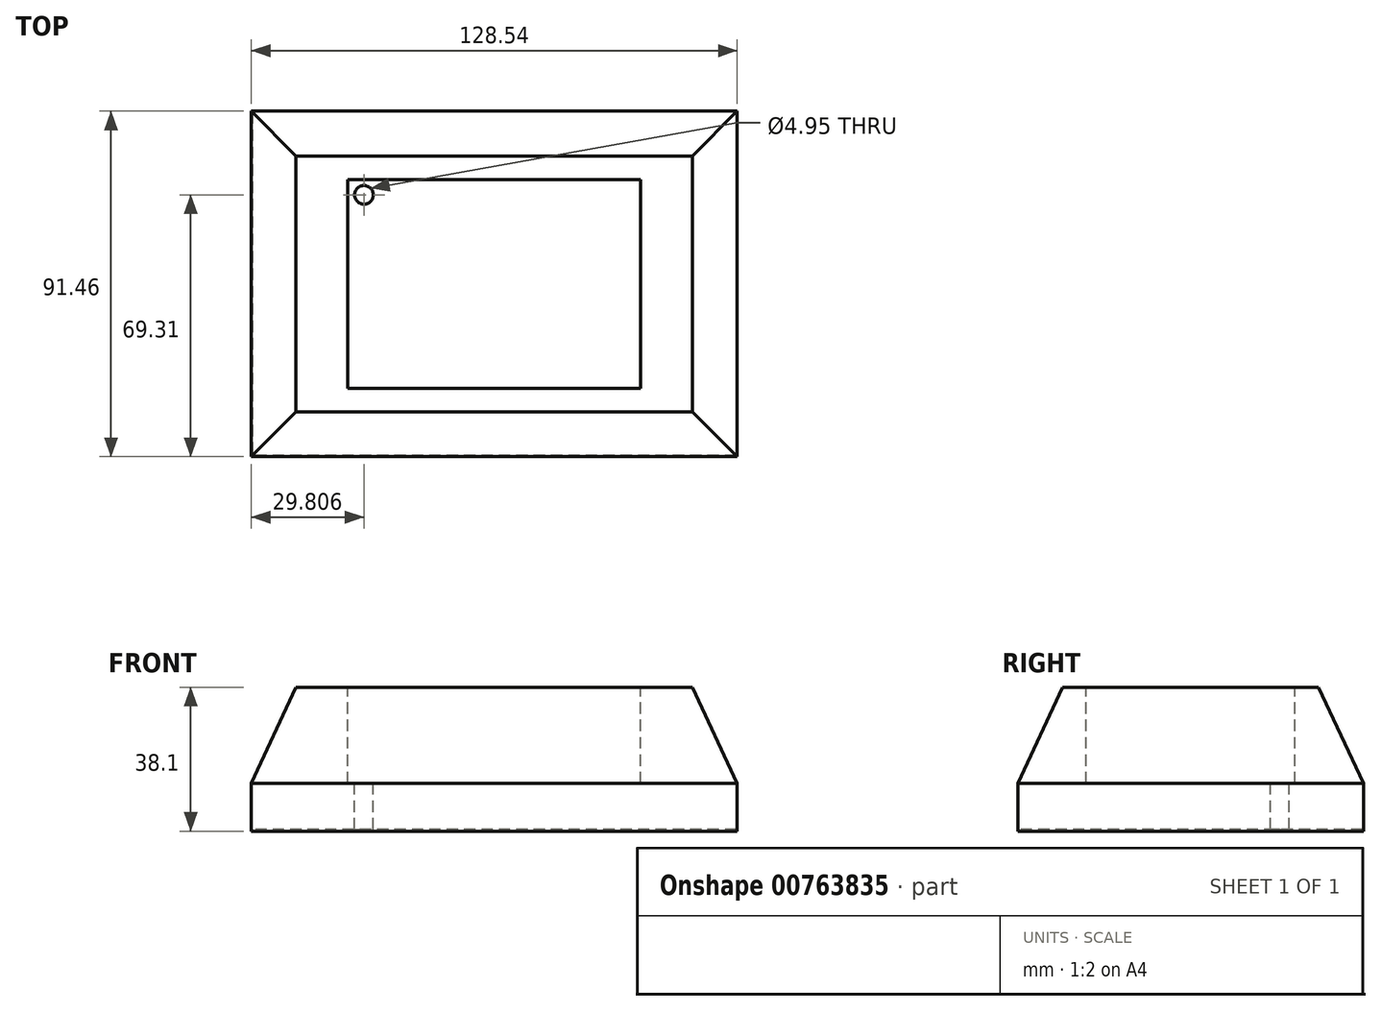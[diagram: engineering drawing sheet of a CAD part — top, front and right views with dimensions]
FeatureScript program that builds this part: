
annotation { "Feature Type Name" : "Feature", "Feature Type Description" : "" }
export const myFeature = defineFeature(function(context is Context, id is Id, definition is map)
    precondition{}
    {
        {
            var Q0;
            Q0=qCreatedBy(makeId("Top.planeOp"),FACE);
            var sketch = newSketch(context, id + "F0", { "sketchPlane" : qUnion([Q0])});
            skLineSegment(sketch, "E0.bottom", {"start": v(64.27, 45.73) * mm, "end": v(-64.27, 45.73) * mm});
            skLineSegment(sketch, "E0.top", {"start": v(64.27, -45.73) * mm, "end": v(-64.27, -45.73) * mm});
            skLineSegment(sketch, "E0.left", {"start": v(64.27, 45.73) * mm, "end": v(64.27, -45.73) * mm});
            skLineSegment(sketch, "E0.right", {"start": v(-64.27, 45.73) * mm, "end": v(-64.27, -45.73) * mm});
            skPoint(sketch, "E0.middle", {"position": v(0, 0) * mm});
            skSolve(sketch);
        }
        {
            var Q0;
            Q0=makeQuery(id+"F0.imprint","IMPRINT",FACE,{"disambiguationData":[TD([[makeQuery(id+"F0.imprint","IMPRINT",EDGE,{"derivedFrom":sQuery(id+"F0.wireOp",EDGE,"E0.bottom")}),1.0]])]});
            extrude(context, id + "F1", {"entities" : qUnion([Q0]), "depth" : 12.7 * mm, "offsetDistance" : 25.4 * mm});
        }
        {
            var Q0;
            Q0=makeQuery(id+"F1.opExtrude","CAP_FACE",FACE,{"disambiguationData":[OSD([sQuery(id+"F0.wireOp",EDGE,"E0.bottom"),sQuery(id+"F0.wireOp",EDGE,"E0.top"),sQuery(id+"F0.wireOp",EDGE,"E0.left"),sQuery(id+"F0.wireOp",EDGE,"E0.right")])],"isStart":false});
            extrude(context, id + "F2", {"entities" : qUnion([Q0]), "operationType" : NewBodyOperationType.ADD, "depth" : 25.4 * mm, "offsetDistance" : 25.4 * mm, "hasDraft" : true, "draftAngle" : 25 * degree, "draftPullDirection" : true});
        }
        {
            var Q0;
            Q0=makeQuery(id+"F1.opExtrude","CAP_FACE",FACE,{"disambiguationData":[OSD([sQuery(id+"F0.wireOp",EDGE,"E0.bottom"),sQuery(id+"F0.wireOp",EDGE,"E0.top"),sQuery(id+"F0.wireOp",EDGE,"E0.left"),sQuery(id+"F0.wireOp",EDGE,"E0.right")])],"isStart":true});
            var sketch = newSketch(context, id + "F3", { "sketchPlane" : qUnion([Q0])});
            skLineSegment(sketch, "E1.0", {"start": v(64.02, -45.48) * mm, "end": v(-64.27, -45.48) * mm});
            skLineSegment(sketch, "E1.1", {"start": v(64.02, -45.48) * mm, "end": v(64.02, 45.48) * mm});
            skLineSegment(sketch, "E1.2", {"start": v(64.02, 45.48) * mm, "end": v(-64.27, 45.48) * mm});
            skLineSegment(sketch, "E2.0", {"start": v(-64.02, -45.73) * mm, "end": v(-64.02, 45.73) * mm});
            skSolve(sketch);
        }
        {
            var Q0;
            Q0 = qSketchRegion(id + "F3", true);
            extrude(context, id + "F4", {"entities" : qUnion([Q0]), "operationType" : NewBodyOperationType.REMOVE, "oppositeDirection" : true, "depth" : 0.5 * mm, "offsetDistance" : 25.4 * mm});
        }
        {
            var Q0;
            Q0=makeQuery(id+"F2.opExtrude","CAP_FACE",FACE,{"disambiguationData":[OSD([sQuery(id+"F0.wireOp",EDGE,"E0.bottom"),sQuery(id+"F0.wireOp",EDGE,"E0.top"),sQuery(id+"F0.wireOp",EDGE,"E0.left"),sQuery(id+"F0.wireOp",EDGE,"E0.right")])],"isStart":false});
            var sketch = newSketch(context, id + "F5", { "sketchPlane" : qUnion([Q0])});
            skLineSegment(sketch, "E3.bottom", {"start": v(38.7, 27.61) * mm, "end": v(-38.7, 27.61) * mm});
            skLineSegment(sketch, "E3.top", {"start": v(38.7, -27.61) * mm, "end": v(-38.7, -27.61) * mm});
            skLineSegment(sketch, "E3.left", {"start": v(38.7, 27.61) * mm, "end": v(38.7, -27.61) * mm});
            skLineSegment(sketch, "E3.right", {"start": v(-38.7, 27.61) * mm, "end": v(-38.7, -27.61) * mm});
            skPoint(sketch, "E3.middle", {"position": v(0, 0) * mm});
            skSolve(sketch);
        }
        {
            var Q0;
            Q0=makeQuery(id+"F5.imprint","IMPRINT",FACE,{"disambiguationData":[TD([[makeQuery(id+"F5.imprint","IMPRINT",EDGE,{"derivedFrom":sQuery(id+"F5.wireOp",EDGE,"E3.bottom")}),1.0]])]});
            extrude(context, id + "F6", {"entities" : qUnion([Q0]), "operationType" : NewBodyOperationType.REMOVE, "oppositeDirection" : true, "depth" : 25.4 * mm, "offsetDistance" : 25.4 * mm});
        }
        {
            var Q0;
            Q0=makeQuery(id+"F6.boolean.opBoolean","COPY",FACE,{"derivedFrom":makeQuery(id+"F6.opExtrude","CAP_FACE",FACE,{"disambiguationData":[OSD([sQuery(id+"F5.wireOp",EDGE,"E3.bottom"),sQuery(id+"F5.wireOp",EDGE,"E3.top"),sQuery(id+"F5.wireOp",EDGE,"E3.left"),sQuery(id+"F5.wireOp",EDGE,"E3.right")])],"isStart":false})});
            var sketch = newSketch(context, id + "F7", { "sketchPlane" : qUnion([Q0])});
            skCircle(sketch, "E4", {"center": v(-34.46, 23.58) * mm, "radius": 2.47 * mm});
            skSolve(sketch);
        }
        {
            var Q0;
            Q0=makeQuery(id+"F7.imprint","IMPRINT",FACE,{"disambiguationData":[TD([[makeQuery(id+"F7.imprint","IMPRINT",EDGE,{"derivedFrom":sQuery(id+"F7.wireOp",EDGE,"E4")}),1.0]])]});
            extrude(context, id + "F8", {"entities" : qUnion([Q0]), "operationType" : NewBodyOperationType.REMOVE, "oppositeDirection" : true, "depth" : 45.57 * mm, "offsetDistance" : 25.4 * mm});
        }
    });
